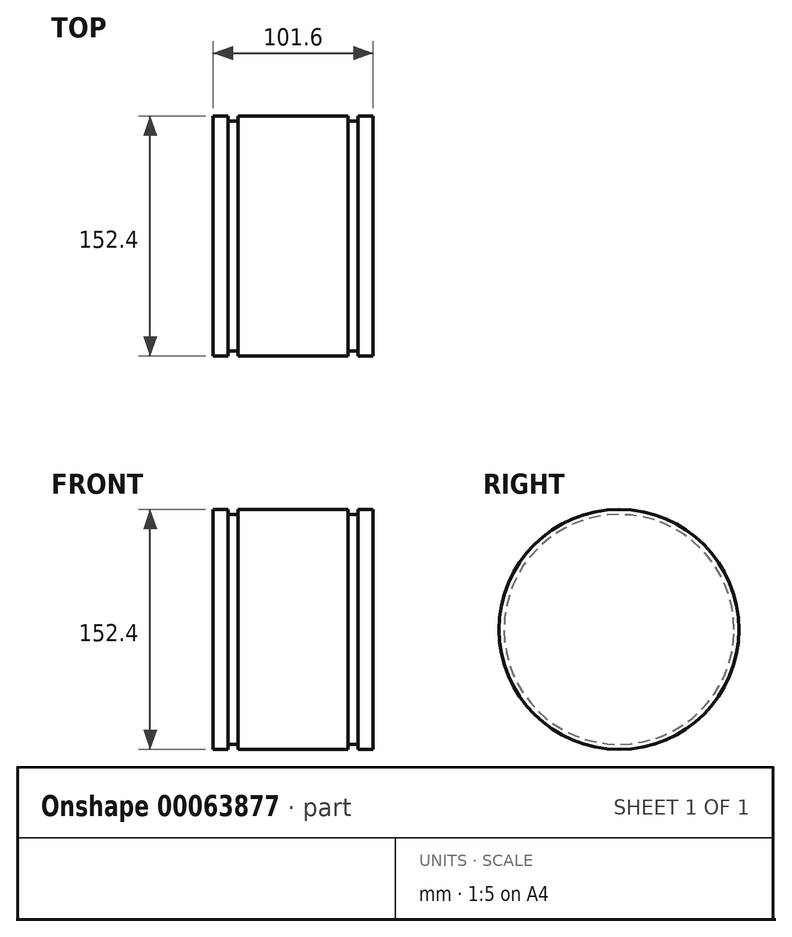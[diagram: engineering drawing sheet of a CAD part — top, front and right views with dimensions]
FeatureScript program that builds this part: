
annotation { "Feature Type Name" : "Feature", "Feature Type Description" : "" }
export const myFeature = defineFeature(function(context is Context, id is Id, definition is map)
    precondition{}
    {
        {
            var Q0;
            Q0=qCreatedBy(makeId("Front.planeOp"),FACE);
            var sketch = newSketch(context, id + "F0", { "sketchPlane" : qUnion([Q0])});
            skLineSegment(sketch, "E0.bottom", {"start": v(0, 0) * mm, "end": v(101.6, 0) * mm});
            skLineSegment(sketch, "E0.top", {"start": v(0, 76.2) * mm, "end": v(9.53, 76.2) * mm});
            skLineSegment(sketch, "E0.left", {"start": v(0, 0) * mm, "end": v(0, 76.2) * mm});
            skLineSegment(sketch, "E0.right", {"start": v(101.6, 0) * mm, "end": v(101.6, 76.2) * mm});
            skLineSegment(sketch, "E1.top", {"start": v(9.52, 73.02) * mm, "end": v(15.87, 73.02) * mm});
            skLineSegment(sketch, "E1.left", {"start": v(9.52, 76.2) * mm, "end": v(9.52, 73.02) * mm});
            skLineSegment(sketch, "E1.right", {"start": v(15.87, 76.2) * mm, "end": v(15.87, 73.02) * mm});
            skLineSegment(sketch, "E2.left", {"start": v(85.72, 76.2) * mm, "end": v(85.72, 73.03) * mm});
            skLineSegment(sketch, "E2.top", {"start": v(85.72, 73.03) * mm, "end": v(92.07, 73.03) * mm});
            skLineSegment(sketch, "E2.right", {"start": v(92.07, 76.2) * mm, "end": v(92.07, 73.03) * mm});
            skLineSegment(sketch, "E3.trimOffspring", {"start": v(92.07, 76.2) * mm, "end": v(101.6, 76.2) * mm});
            skLineSegment(sketch, "E4.trimOffspring", {"start": v(15.87, 76.2) * mm, "end": v(85.72, 76.2) * mm});
            skSolve(sketch);
        }
        {
            var Q0;
            Q0 = qSketchRegion(id + "F0", true);
            var Q1;
            Q1=sQuery(id+"F0.wireOp",EDGE,"E0.bottom");
            revolve(context, id + "F1", {"entities" : qUnion([Q0]), "axis" : qUnion([Q1]), "revolveType" : RevolveType.FULL});
        }
    });
